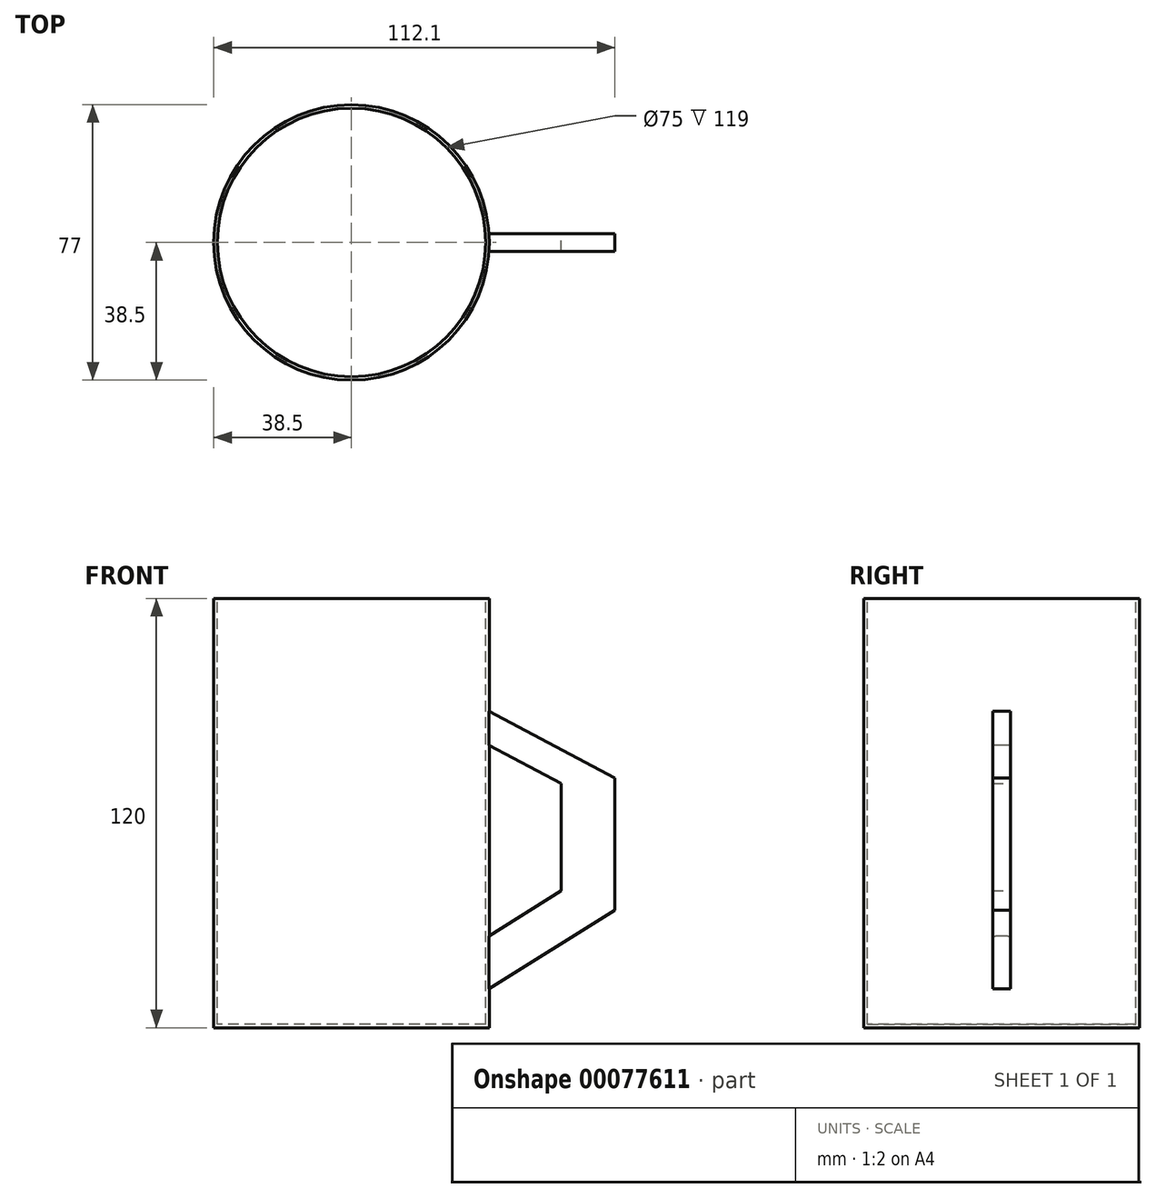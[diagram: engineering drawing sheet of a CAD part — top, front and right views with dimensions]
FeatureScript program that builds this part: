
annotation { "Feature Type Name" : "Feature", "Feature Type Description" : "" }
export const myFeature = defineFeature(function(context is Context, id is Id, definition is map)
    precondition{}
    {
        {
            var Q0;
            Q0=qCreatedBy(makeId("Right.planeOp"),FACE);
            var sketch = newSketch(context, id + "F0", { "sketchPlane" : qUnion([Q0])});
            skLineSegment(sketch, "E0", {"start": v(0, 0) * mm, "end": v(-38.5, 0) * mm});
            skLineSegment(sketch, "E1", {"start": v(-38.5, 0) * mm, "end": v(-38.5, 120) * mm});
            skLineSegment(sketch, "E2", {"start": v(-38.5, 120) * mm, "end": v(0, 120) * mm});
            skLineSegment(sketch, "E3", {"start": v(0, 120) * mm, "end": v(0, 0) * mm});
            skSolve(sketch);
        }
        {
            var Q0;
            Q0=makeQuery(id+"F0.imprint","IMPRINT",FACE,{"disambiguationData":[TD([[makeQuery(id+"F0.imprint","IMPRINT",EDGE,{"derivedFrom":sQuery(id+"F0.wireOp",EDGE,"E0")}),-1.0]])]});
            var Q1;
            Q1=sQuery(id+"F0.wireOp",EDGE,"E3");
            revolve(context, id + "F1", {"entities" : qUnion([Q0]), "axis" : qUnion([Q1]), "revolveType" : RevolveType.FULL});
        }
        {
            var Q0;
            Q0=makeQuery(id+"F1.opRevolve","SWEPT_FACE",FACE,{"disambiguationData":[OSD([sQuery(id+"F0.wireOp",EDGE,"E2")])]});
            shell(context, id + "F2", {"entities" : qUnion([Q0]), "thickness" : 1 * mm});
        }
        {
            var Q0;
            Q0=qCreatedBy(makeId("Front.planeOp"),FACE);
            var sketch = newSketch(context, id + "F3", { "sketchPlane" : qUnion([Q0])});
            skLineSegment(sketch, "E4", {"start": v(38.35, 88.51) * mm, "end": v(73.6, 69.77) * mm});
            skLineSegment(sketch, "E5", {"start": v(73.6, 69.77) * mm, "end": v(73.6, 32.86) * mm});
            skLineSegment(sketch, "E6", {"start": v(73.6, 32.86) * mm, "end": v(37.89, 10.55) * mm});
            skLineSegment(sketch, "E7", {"start": v(37.89, 10.55) * mm, "end": v(37.89, 25.3) * mm});
            skLineSegment(sketch, "E8", {"start": v(37.89, 25.3) * mm, "end": v(58.6, 38.25) * mm});
            skLineSegment(sketch, "E9", {"start": v(58.6, 38.25) * mm, "end": v(58.6, 68.25) * mm});
            skLineSegment(sketch, "E10", {"start": v(58.6, 68.25) * mm, "end": v(38.18, 79.1) * mm});
            skLineSegment(sketch, "E11", {"start": v(38.18, 79.1) * mm, "end": v(38.35, 88.51) * mm});
            skSolve(sketch);
        }
        {
            var Q0;
            Q0=makeQuery(id+"F3.imprint","IMPRINT",FACE,{"disambiguationData":[TD([[makeQuery(id+"F3.imprint","IMPRINT",EDGE,{"derivedFrom":sQuery(id+"F3.wireOp",EDGE,"E4")}),-1.0]])]});
            extrude(context, id + "F4", {"entities" : qUnion([Q0]), "operationType" : NewBodyOperationType.ADD, "endBound" : BoundingType.SYMMETRIC, "depth" : 5 * mm});
        }
    });
